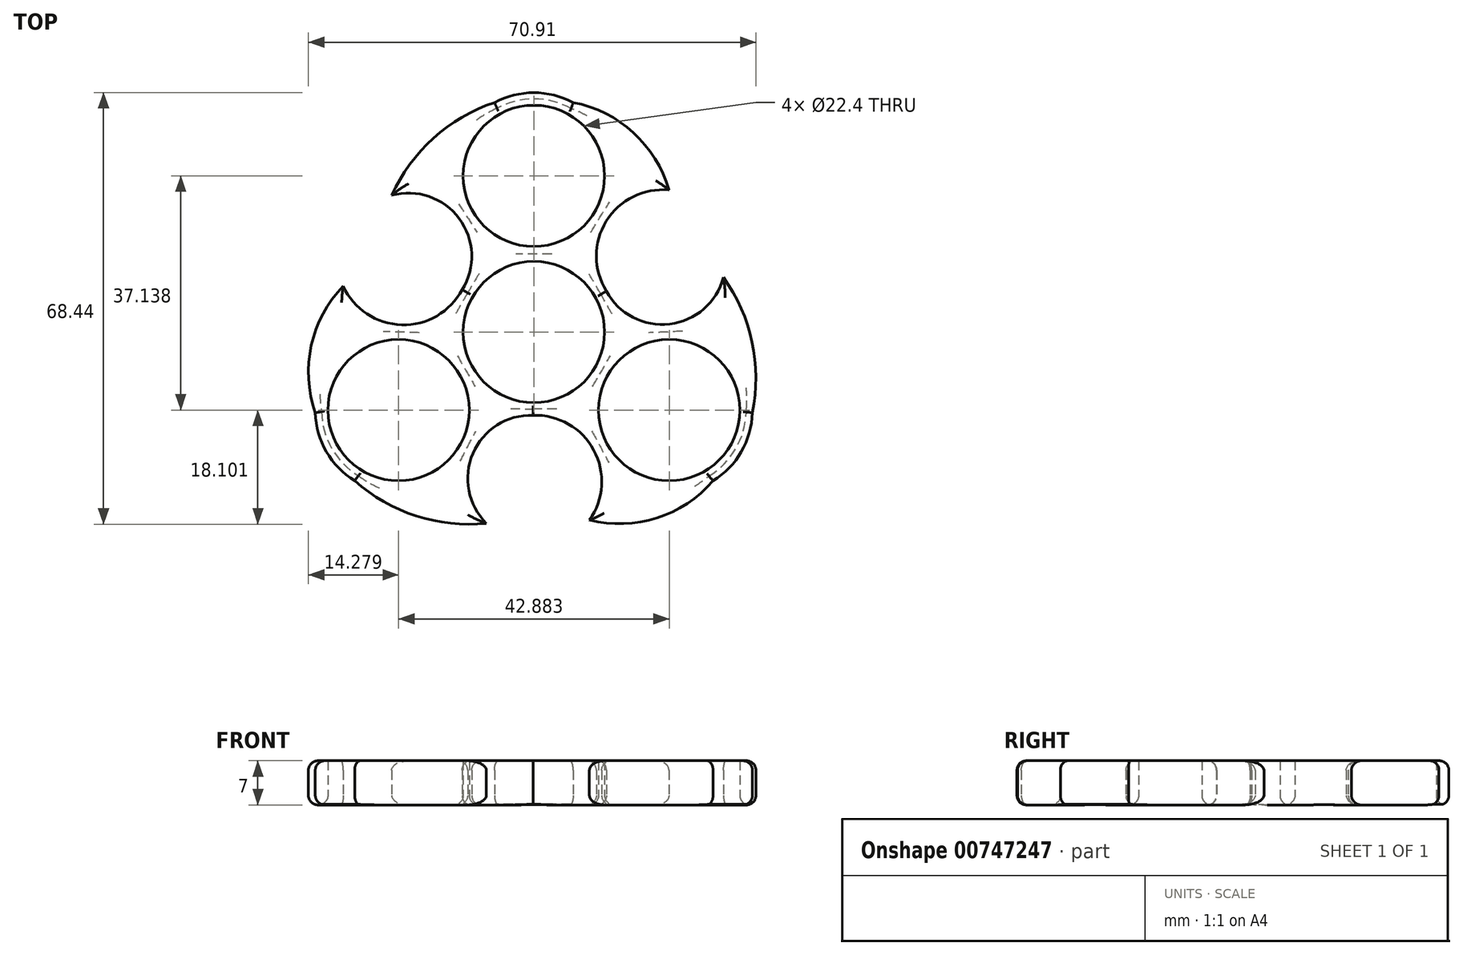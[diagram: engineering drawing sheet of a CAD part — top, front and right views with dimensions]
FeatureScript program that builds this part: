
annotation { "Feature Type Name" : "Feature", "Feature Type Description" : "" }
export const myFeature = defineFeature(function(context is Context, id is Id, definition is map)
    precondition{}
    {
        {
            var Q0;
            Q0=qCreatedBy(makeId("Top.planeOp"),FACE);
            var sketch = newSketch(context, id + "F0", { "sketchPlane" : qUnion([Q0])});
            skCircle(sketch, "E0", {"center": v(0, 0) * mm, "radius": 11.2 * mm});
            skArc(sketch, "E1", {"start": v(-11.23, 6.93) * mm, "mid": v(-11.43, 6.6) * mm, "end": v(-11.62, 6.25) * mm});
            skCircle(sketch, "E2", {"center": v(0, 24.76) * mm, "radius": 11.2 * mm});
            skArc(sketch, "E3", {"start": v(-6.23, 36.4) * mm, "mid": v(-15.92, 30.74) * mm, "end": v(-22.52, 21.68) * mm});
            skCircle(sketch, "E4.1.0", {"center": v(-21.44, -12.38) * mm, "radius": 11.2 * mm});
            skArc(sketch, "E4.1.1", {"start": v(-28.4, -23.6) * mm, "mid": v(-18.66, -29.15) * mm, "end": v(-7.52, -30.34) * mm});
            skArc(sketch, "E4.1.2", {"start": v(-34.63, -12.8) * mm, "mid": v(-32.87, -18.98) * mm, "end": v(-28.4, -23.6) * mm});
            skCircle(sketch, "E4.2.0", {"center": v(21.44, -12.38) * mm, "radius": 11.2 * mm});
            skArc(sketch, "E4.2.1", {"start": v(34.63, -12.8) * mm, "mid": v(34.58, -1.59) * mm, "end": v(30.04, 8.66) * mm});
            skArc(sketch, "E4.2.2", {"start": v(28.4, -23.6) * mm, "mid": v(32.87, -18.98) * mm, "end": v(34.63, -12.8) * mm});
            skArc(sketch, "E5", {"start": v(21.4, 22.52) * mm, "mid": v(15.78, 31.6) * mm, "end": v(6.23, 36.4) * mm});
            skArc(sketch, "E6.1.0", {"start": v(-30.2, 7.27) * mm, "mid": v(-35.26, -2.13) * mm, "end": v(-34.63, -12.8) * mm});
            skArc(sketch, "E6.2.0", {"start": v(8.8, -29.8) * mm, "mid": v(19.48, -29.47) * mm, "end": v(28.4, -23.6) * mm});
            skArc(sketch, "E7", {"start": v(-11.36, 6.71) * mm, "mid": v(-11.84, 18) * mm, "end": v(-22.52, 21.68) * mm});
            skArc(sketch, "E8", {"start": v(-30.2, 7.27) * mm, "mid": v(-20.96, 1.14) * mm, "end": v(-11.36, 6.71) * mm});
            skArc(sketch, "E9.1.0", {"start": v(-0.13, -13.2) * mm, "mid": v(-9.67, -19.25) * mm, "end": v(-7.52, -30.34) * mm});
            skArc(sketch, "E9.1.1", {"start": v(8.8, -29.8) * mm, "mid": v(9.5, -18.72) * mm, "end": v(-0.13, -13.2) * mm});
            skArc(sketch, "E9.2.0", {"start": v(11.5, 6.48) * mm, "mid": v(21.5, 1.25) * mm, "end": v(30.04, 8.66) * mm});
            skArc(sketch, "E9.2.1", {"start": v(21.4, 22.52) * mm, "mid": v(11.47, 17.58) * mm, "end": v(11.5, 6.48) * mm});
            skArc(sketch, "E10.trimOffspring", {"start": v(6.23, 36.4) * mm, "mid": v(0, 37.96) * mm, "end": v(-6.23, 36.4) * mm});
            skArc(sketch, "E11.trimOffspring", {"start": v(11.62, 6.26) * mm, "mid": v(11.43, 6.6) * mm, "end": v(11.23, 6.94) * mm});
            skArc(sketch, "E12.trimOffspring", {"start": v(-0.39, -13.2) * mm, "mid": v(0, -13.2) * mm, "end": v(0.4, -13.2) * mm});
            skSolve(sketch);
        }
        {
            var Q0;
            Q0=makeQuery(id+"F0.imprint","IMPRINT",FACE,{"disambiguationData":[TD([[makeQuery(id+"F0.imprint","IMPRINT",EDGE,{"derivedFrom":sQuery(id+"F0.wireOp",EDGE,"E0")}),-1.0]])]});
            extrude(context, id + "F1", {"entities" : qUnion([Q0]), "depth" : 7 * mm, "offsetDistance" : 25 * mm});
        }
        {
            var Q0;
            Q0=makeQuery(id+"F1.opExtrude","CAP_EDGE",EDGE,{"disambiguationData":[OSD([sQuery(id+"F0.wireOp",EDGE,"E9.2.0")])],"isStart":false});
            var Q1;
            Q1=makeQuery(id+"F1.opExtrude","CAP_EDGE",EDGE,{"disambiguationData":[OSD([sQuery(id+"F0.wireOp",EDGE,"E9.2.1")])],"isStart":false});
            var Q2;
            Q2=makeQuery(id+"F1.opExtrude","CAP_EDGE",EDGE,{"disambiguationData":[OSD([sQuery(id+"F0.wireOp",EDGE,"E5")])],"isStart":false});
            var Q3;
            Q3=makeQuery(id+"F1.opExtrude","CAP_EDGE",EDGE,{"disambiguationData":[OSD([sQuery(id+"F0.wireOp",EDGE,"E10.trimOffspring")])],"isStart":false});
            var Q4;
            Q4=makeQuery(id+"F1.opExtrude","CAP_EDGE",EDGE,{"disambiguationData":[OSD([sQuery(id+"F0.wireOp",EDGE,"E3")])],"isStart":false});
            var Q5;
            Q5=makeQuery(id+"F1.opExtrude","CAP_EDGE",EDGE,{"disambiguationData":[OSD([sQuery(id+"F0.wireOp",EDGE,"E7")])],"isStart":false});
            var Q6;
            Q6=makeQuery(id+"F1.opExtrude","CAP_EDGE",EDGE,{"disambiguationData":[OSD([sQuery(id+"F0.wireOp",EDGE,"E8")])],"isStart":false});
            var Q7;
            Q7=makeQuery(id+"F1.opExtrude","CAP_EDGE",EDGE,{"disambiguationData":[OSD([sQuery(id+"F0.wireOp",EDGE,"E6.1.0")])],"isStart":false});
            var Q8;
            Q8=makeQuery(id+"F1.opExtrude","CAP_EDGE",EDGE,{"disambiguationData":[OSD([sQuery(id+"F0.wireOp",EDGE,"E4.1.2")])],"isStart":false});
            var Q9;
            Q9=makeQuery(id+"F1.opExtrude","CAP_EDGE",EDGE,{"disambiguationData":[OSD([sQuery(id+"F0.wireOp",EDGE,"E4.1.1")])],"isStart":false});
            var Q10;
            Q10=makeQuery(id+"F1.opExtrude","CAP_EDGE",EDGE,{"disambiguationData":[OSD([sQuery(id+"F0.wireOp",EDGE,"E9.1.0")])],"isStart":false});
            var Q11;
            Q11=makeQuery(id+"F1.opExtrude","CAP_EDGE",EDGE,{"disambiguationData":[OSD([sQuery(id+"F0.wireOp",EDGE,"E9.1.1")])],"isStart":false});
            var Q12;
            Q12=makeQuery(id+"F1.opExtrude","CAP_EDGE",EDGE,{"disambiguationData":[OSD([sQuery(id+"F0.wireOp",EDGE,"E6.2.0")])],"isStart":false});
            var Q13;
            Q13=makeQuery(id+"F1.opExtrude","CAP_EDGE",EDGE,{"disambiguationData":[OSD([sQuery(id+"F0.wireOp",EDGE,"E4.2.2")])],"isStart":false});
            var Q14;
            Q14=makeQuery(id+"F1.opExtrude","CAP_EDGE",EDGE,{"disambiguationData":[OSD([sQuery(id+"F0.wireOp",EDGE,"E4.2.1")])],"isStart":false});
            fillet(context, id + "F2", {"entities" : qUnion([Q0, Q1, Q2, Q3, Q4, Q5, Q6, Q7, Q8, Q9, Q10, Q11, Q12, Q13, Q14]), "radius" : 1.5 * mm, "tangentPropagation" : true, "allowEdgeOverflow" : false});
        }
        {
            var Q0;
            Q0=makeQuery(id+"F1.opExtrude","CAP_FACE",FACE,{"disambiguationData":[OSD([sQuery(id+"F0.wireOp",EDGE,"E0"),sQuery(id+"F0.wireOp",EDGE,"E2"),sQuery(id+"F0.wireOp",EDGE,"E3"),sQuery(id+"F0.wireOp",EDGE,"E4.1.0"),sQuery(id+"F0.wireOp",EDGE,"E4.1.1"),sQuery(id+"F0.wireOp",EDGE,"E4.1.2"),sQuery(id+"F0.wireOp",EDGE,"E4.2.0"),sQuery(id+"F0.wireOp",EDGE,"E4.2.1"),sQuery(id+"F0.wireOp",EDGE,"E4.2.2"),sQuery(id+"F0.wireOp",EDGE,"E5"),sQuery(id+"F0.wireOp",EDGE,"E6.1.0"),sQuery(id+"F0.wireOp",EDGE,"E6.2.0"),sQuery(id+"F0.wireOp",EDGE,"E7"),sQuery(id+"F0.wireOp",EDGE,"E8"),sQuery(id+"F0.wireOp",EDGE,"E9.1.0"),sQuery(id+"F0.wireOp",EDGE,"E9.1.1"),sQuery(id+"F0.wireOp",EDGE,"E9.2.0"),sQuery(id+"F0.wireOp",EDGE,"E9.2.1"),sQuery(id+"F0.wireOp",EDGE,"E10.trimOffspring")])],"isStart":true});
            fillet(context, id + "F3", {"entities" : qUnion([Q0]), "radius" : 1.5 * mm, "tangentPropagation" : true, "allowEdgeOverflow" : false});
        }
    });
